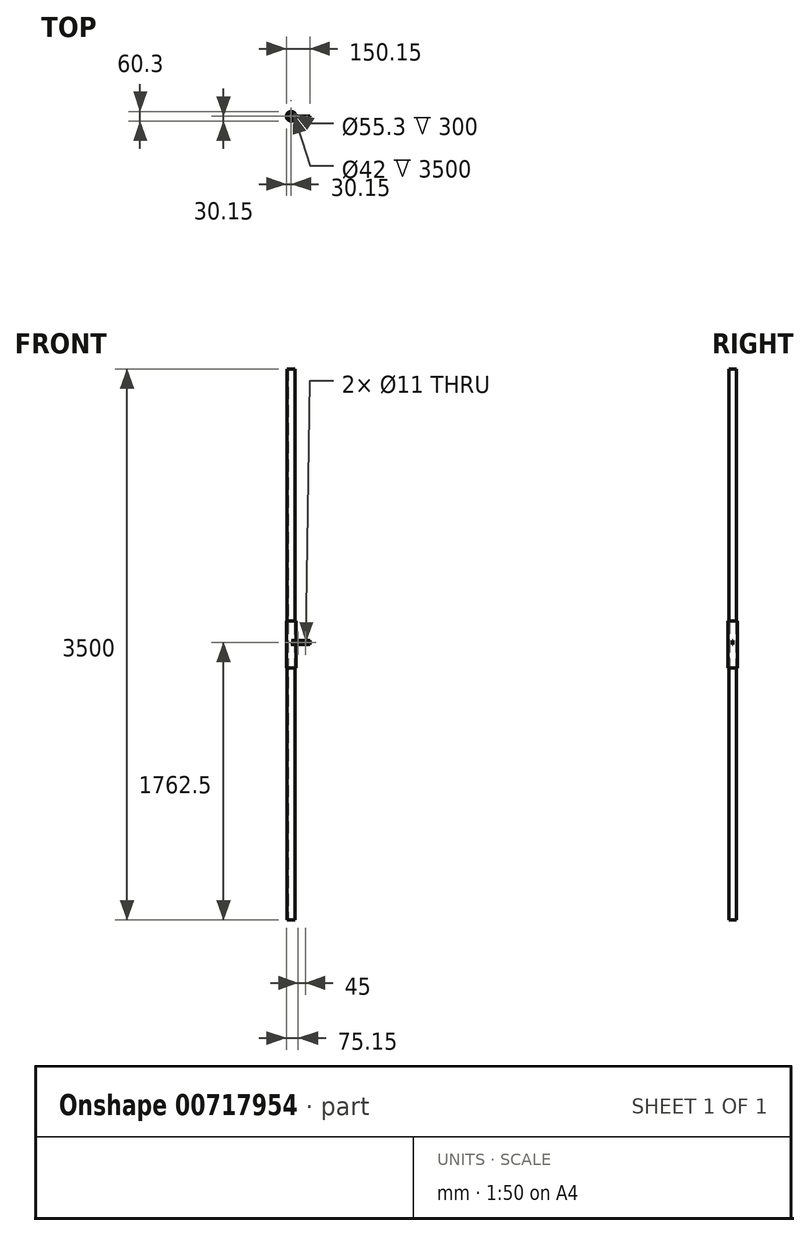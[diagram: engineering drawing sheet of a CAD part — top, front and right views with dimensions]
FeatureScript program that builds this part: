
annotation { "Feature Type Name" : "Feature", "Feature Type Description" : "" }
export const myFeature = defineFeature(function(context is Context, id is Id, definition is map)
    precondition{}
    {
        {
            var Q0;
            Q0=qCreatedBy(makeId("Top.planeOp"),FACE);
            var sketch = newSketch(context, id + "F0", { "sketchPlane" : qUnion([Q0])});
            skCircle(sketch, "E0", {"center": v(0, 0) * mm, "radius": 25 * mm});
            skCircle(sketch, "E1", {"center": v(0, 0) * mm, "radius": 21 * mm});
            skSolve(sketch);
        }
        {
            var Q0;
            Q0=makeQuery(id+"F0.imprint","IMPRINT",FACE,{"disambiguationData":[TD([[makeQuery(id+"F0.imprint","IMPRINT",EDGE,{"derivedFrom":sQuery(id+"F0.wireOp",EDGE,"E0")}),1.0]])]});
            extrude(context, id + "F1", {"entities" : qUnion([Q0]), "endBound" : BoundingType.SYMMETRIC, "depth" : 3500 * mm, "offsetDistance" : 25 * mm});
        }
        {
            var Q0;
            Q0=qCreatedBy(makeId("Top.planeOp"),FACE);
            var sketch = newSketch(context, id + "F2", { "sketchPlane" : qUnion([Q0])});
            skCircle(sketch, "E2", {"center": v(0, 0) * mm, "radius": 30.15 * mm});
            skCircle(sketch, "E3", {"center": v(0, 0) * mm, "radius": 27.65 * mm});
            skSolve(sketch);
        }
        {
            var Q0;
            Q0=makeQuery(id+"F2.imprint","IMPRINT",FACE,{"disambiguationData":[TD([[makeQuery(id+"F2.imprint","IMPRINT",EDGE,{"derivedFrom":sQuery(id+"F2.wireOp",EDGE,"E2")}),1.0]])]});
            extrude(context, id + "F3", {"entities" : qUnion([Q0]), "endBound" : BoundingType.SYMMETRIC, "depth" : 300 * mm, "offsetDistance" : 25 * mm});
        }
        {
            var Q0;
            Q0=qCreatedBy(makeId("Front.planeOp"),FACE);
            var sketch = newSketch(context, id + "F4", { "sketchPlane" : qUnion([Q0])});
            skLineSegment(sketch, "E4", {"start": v(0, 0) * mm, "end": v(120, 0) * mm});
            skLineSegment(sketch, "E5", {"start": v(120, 0) * mm, "end": v(120, 25) * mm});
            skLineSegment(sketch, "E6", {"start": v(120, 25) * mm, "end": v(3.07, 25) * mm});
            skLineSegment(sketch, "E7", {"start": v(3.07, 25) * mm, "end": v(0, 0) * mm});
            skLineSegment(sketch, "E8", {"start": v(120, 12.5) * mm, "end": v(1.53, 12.5) * mm, "construction": true});
            skLineSegment(sketch, "E9", {"start": v(90, 43.68) * mm, "end": v(90, -27.78) * mm, "construction": true});
            skLineSegment(sketch, "E10", {"start": v(45, 43.1) * mm, "end": v(45, -31.44) * mm, "construction": true});
            skCircle(sketch, "E11", {"center": v(90, 12.5) * mm, "radius": 5.5 * mm});
            skCircle(sketch, "E12", {"center": v(45, 12.5) * mm, "radius": 5.5 * mm});
            skSolve(sketch);
        }
        {
            var Q0;
            Q0=makeQuery(id+"F4.imprint","IMPRINT",FACE,{"disambiguationData":[TD([[makeQuery(id+"F4.imprint","IMPRINT",EDGE,{"derivedFrom":sQuery(id+"F4.wireOp",EDGE,"E4")}),1.0]])]});
            extrude(context, id + "F5", {"entities" : qUnion([Q0]), "endBound" : BoundingType.SYMMETRIC, "depth" : 4 * mm, "offsetDistance" : 25 * mm});
        }
    });
